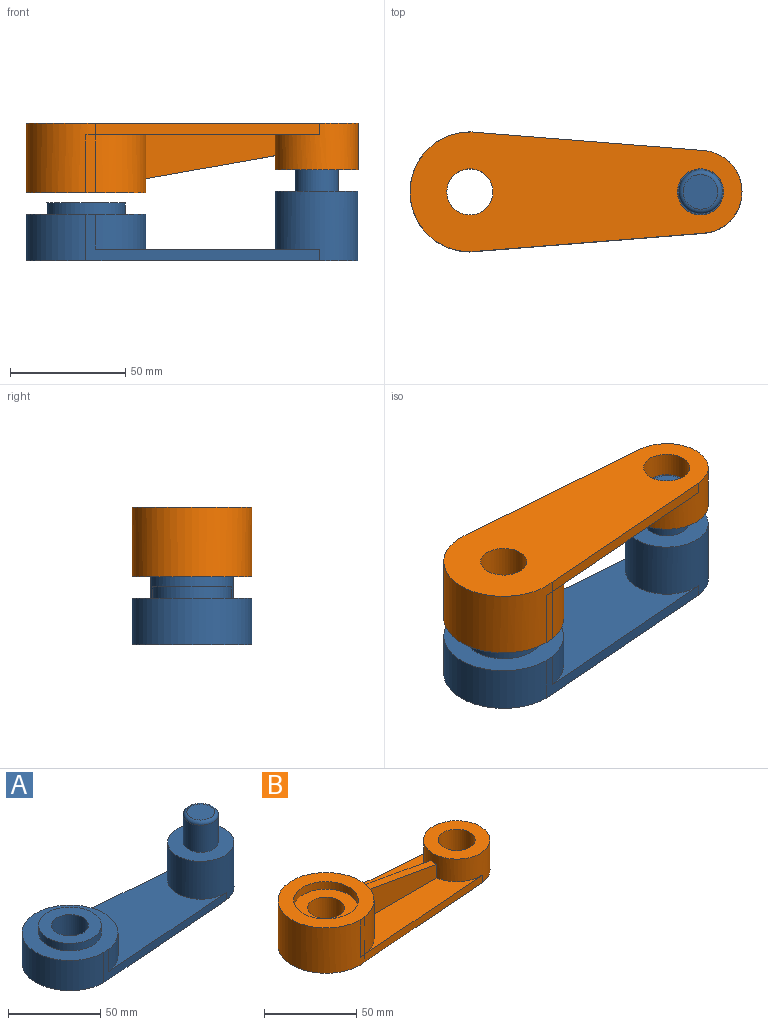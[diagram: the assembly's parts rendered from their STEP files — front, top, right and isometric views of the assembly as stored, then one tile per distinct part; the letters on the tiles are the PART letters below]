
ASSEMBLY  parts=2 mates=1
PART A: 15 faces, bbox 144x52x50 mm
  f0: cylinder r=26mm len=51.35mm, axis (0,0,-1), area 1101.6mm2, adj f1,f3,f7,f9
  f1: plane 101.43x20mm, normal (0.08,1,0), area 570.5mm2, adj f0,f2,f4,f5,f7,f9
  f2: cylinder r=26mm len=52mm, axis (0,0,-1), area 1633.6mm2, adj f1,f3,f4,f9
  f3: plane 101.43x20mm, normal (0.08,-1,0), area 570.5mm2, adj f0,f2,f4,f5,f7,f9
  f4: plane 144x52mm, normal (0,0,-1), area 5662.4mm2, adj f1,f2,f3,f5,f11
  f5: cylinder r=18mm len=36mm, axis (0,0,-1), area 3095.9mm2, adj f1,f3,f4,f6,f7
  f6: plane 36x36mm, normal (0,0,1), area 734.3mm2, adj f5,f12
  f7: plane 97.32x51.35mm, normal (0,0,1), area 2835.4mm2, adj f0,f1,f3,f5
  f8: cylinder r=17mm len=34mm, axis (0,0,1), area 534.1mm2, adj f9,f10
  f9: plane 52x52mm, normal (0,0,1), area 1215.3mm2, adj f0,f1,f2,f3,f8
  f10: plane 34x34mm, normal (0,0,1), area 593.8mm2, adj f8,f11
  f11: cylinder r=10mm len=25mm, axis (0,0,1), area 1570.8mm2, adj f4,f10
  f12: cylinder r=9.5mm len=19mm, axis (0,0,-1), area 1074.4mm2, adj f6,f14
  f13: plane 15x15mm, normal (0,0,1), area 176.7mm2, adj f14
  f14: torus R=7.5mm, axis (0,0,1), area 173.2mm2, adj f12,f13
PART B: 21 faces, bbox 144x52x30 mm
  f0: cylinder r=26mm len=51.35mm, axis (0,0,-1), area 1740.8mm2, adj f1,f3,f4,f6,f7,f14,f15,f16
  f1: plane 25x4.1mm, normal (0.08,1,0), area 102.9mm2, adj f0,f2,f4,f11
  f2: cylinder r=26mm len=52mm, axis (0,0,-1), area 2491.7mm2, adj f1,f3,f4,f5,f8,f11,f12,f13
  f3: plane 25x4.1mm, normal (0.08,-1,0), area 102.9mm2, adj f0,f2,f4,f8
  f4: plane 52x52mm, normal (0,0,1), area 1161.2mm2, adj f0,f1,f2,f3,f17
  f5: plane 144x52mm, normal (0,0,-1), area 5348.6mm2, adj f2,f9,f12,f13,f19,f20
  f6: plane 97.32x23.17mm, normal (0,0,1), area 1277.4mm2, adj f0,f9,f13,f15
  f7: plane 97.32x23.17mm, normal (0,0,1), area 1277.4mm2, adj f0,f9,f12,f14
  f8: plane 4.1x0.33mm, normal (0,0,1), area 0.2mm2, adj f2,f3
  f9: cylinder r=18mm len=36mm, axis (0,0,-1), area 1919.8mm2, adj f5,f6,f7,f10,f12,f13,f14,f15
  f10: plane 36x36mm, normal (0,0,1), area 703.7mm2, adj f9,f20
  f11: plane 4.1x0.33mm, normal (0,0,1), area 0.2mm2, adj f1,f2
  f12: plane 97.32x7.73mm, normal (0.08,-1,0), area 488.1mm2, adj f2,f5,f7,f9
  f13: plane 97.32x7.73mm, normal (0.08,1,0), area 488.1mm2, adj f2,f5,f6,f9
  f14: plane 56.3x19.02mm, normal (0,-1,0), area 787.9mm2, adj f0,f7,f9,f16
  f15: plane 56.3x19.02mm, normal (0,1,0), area 787.9mm2, adj f0,f6,f9,f16
  f16: plane 56.3x10.05mm, normal (0.18,0,0.98), area 284.9mm2, adj f0,f9,f14,f15
  f17: cylinder r=17.5mm len=35mm, axis (0,0,1), area 549.8mm2, adj f4,f18
  f18: plane 35x35mm, normal (0,0,1), area 648mm2, adj f17,f19
  f19: cylinder r=10mm len=25mm, axis (0,0,1), area 1570.8mm2, adj f5,f18
  f20: cylinder r=10mm len=20mm, axis (0,0,1), area 1256.6mm2, adj f5,f10
PLACE A t=(-58.09,6.59,-4.64)mm
PLACE B rot(axis=(1,0,0),180deg) t=(-58.09,6.59,54.86)mm
MATE slider B.f0 <-> A.f0  axis (0,0,-1) through (-58.09,6.59,27.36)mm
